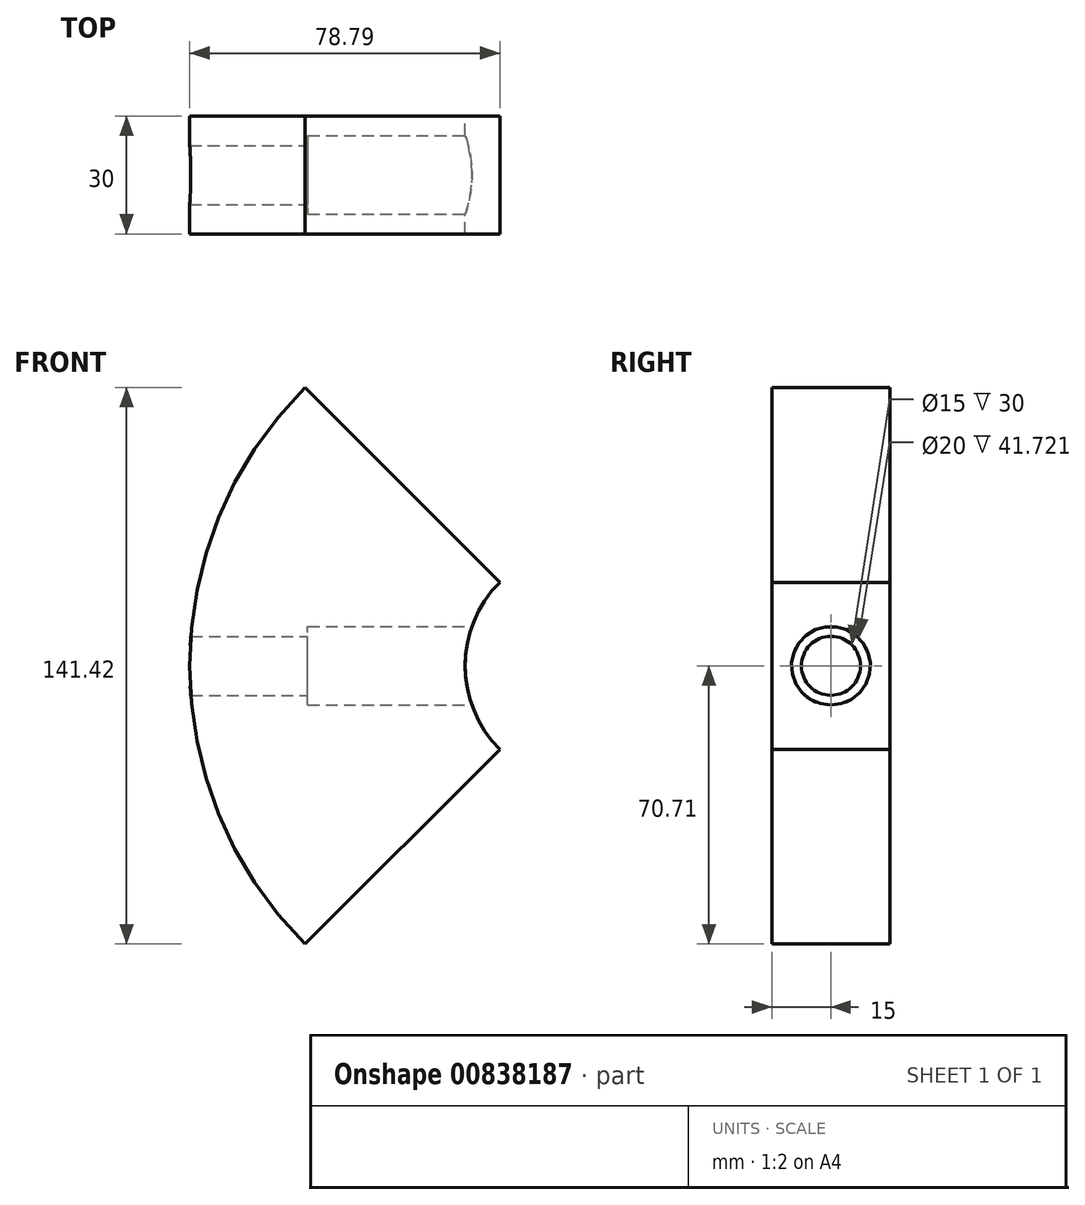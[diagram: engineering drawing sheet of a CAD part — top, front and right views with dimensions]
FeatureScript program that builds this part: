
annotation { "Feature Type Name" : "Feature", "Feature Type Description" : "" }
export const myFeature = defineFeature(function(context is Context, id is Id, definition is map)
    precondition{}
    {
        {
            var Q0;
            Q0=qCreatedBy(makeId("Front.planeOp"),FACE);
            var sketch = newSketch(context, id + "F0", { "sketchPlane" : qUnion([Q0])});
            skArc(sketch, "E0", {"start": v(-21.21, 21.21) * mm, "mid": v(-30, 0) * mm, "end": v(-21.21, -21.21) * mm});
            skArc(sketch, "E1", {"start": v(-70.71, 70.71) * mm, "mid": v(-100, 0) * mm, "end": v(-70.71, -70.71) * mm});
            skLineSegment(sketch, "E2.1.0", {"start": v(-70.71, 70.71) * mm, "end": v(-21.21, 21.21) * mm});
            skLineSegment(sketch, "E2.2.0", {"start": v(-100, 0) * mm, "end": v(-30, 0) * mm});
            skLineSegment(sketch, "E2.3.0", {"start": v(-70.71, -70.71) * mm, "end": v(-21.21, -21.21) * mm});
            skLineSegment(sketch, "E2.6.0", {"start": v(-30, 0) * mm, "end": v(-100, 0) * mm});
            skLineSegment(sketch, "E2.7.0", {"start": v(21.21, 21.21) * mm, "end": v(0, 0) * mm});
            skPoint(sketch, "E3.orphan", {"position": v(0, 100) * mm});
            skPoint(sketch, "E4.orphan", {"position": v(100, 0) * mm});
            skPoint(sketch, "E5.orphan", {"position": v(70.71, 70.71) * mm});
            skLineSegment(sketch, "E6.trimOffspring", {"start": v(-21.21, 21.21) * mm, "end": v(-70.71, 70.71) * mm});
            skLineSegment(sketch, "E7.trimOffspring", {"start": v(-21.21, -21.21) * mm, "end": v(-70.71, -70.71) * mm});
            skSolve(sketch);
        }
        {
            var Q0;
            Q0 = qSketchRegion(id + "F0", true);
            extrude(context, id + "F1", {"entities" : qUnion([Q0]), "endBound" : BoundingType.SYMMETRIC, "depth" : 30 * mm, "offsetDistance" : 25 * mm});
        }
        {
            var Q0;
            Q0=qCreatedBy(makeId("Right.planeOp"),FACE);
            var sketch = newSketch(context, id + "F2", { "sketchPlane" : qUnion([Q0])});
            skCircle(sketch, "E8", {"center": v(0, 0) * mm, "radius": 7.5 * mm});
            skSolve(sketch);
        }
        {
            var Q0;
            Q0 = qSketchRegion(id + "F2", true);
            extrude(context, id + "F3", {"entities" : qUnion([Q0]), "operationType" : NewBodyOperationType.REMOVE, "oppositeDirection" : true, "depth" : 107.34 * mm, "offsetDistance" : 25 * mm});
        }
        {
            var Q0;
            Q0=qCreatedBy(makeId("Right.planeOp"),FACE);
            var sketch = newSketch(context, id + "F4", { "sketchPlane" : qUnion([Q0])});
            skCircle(sketch, "E9", {"center": v(0, 0) * mm, "radius": 10 * mm});
            skSolve(sketch);
        }
        {
            var Q0;
            Q0 = qSketchRegion(id + "F4", true);
            extrude(context, id + "F5", {"entities" : qUnion([Q0]), "operationType" : NewBodyOperationType.REMOVE, "oppositeDirection" : true, "depth" : 70 * mm, "offsetDistance" : 25 * mm});
        }
    });
